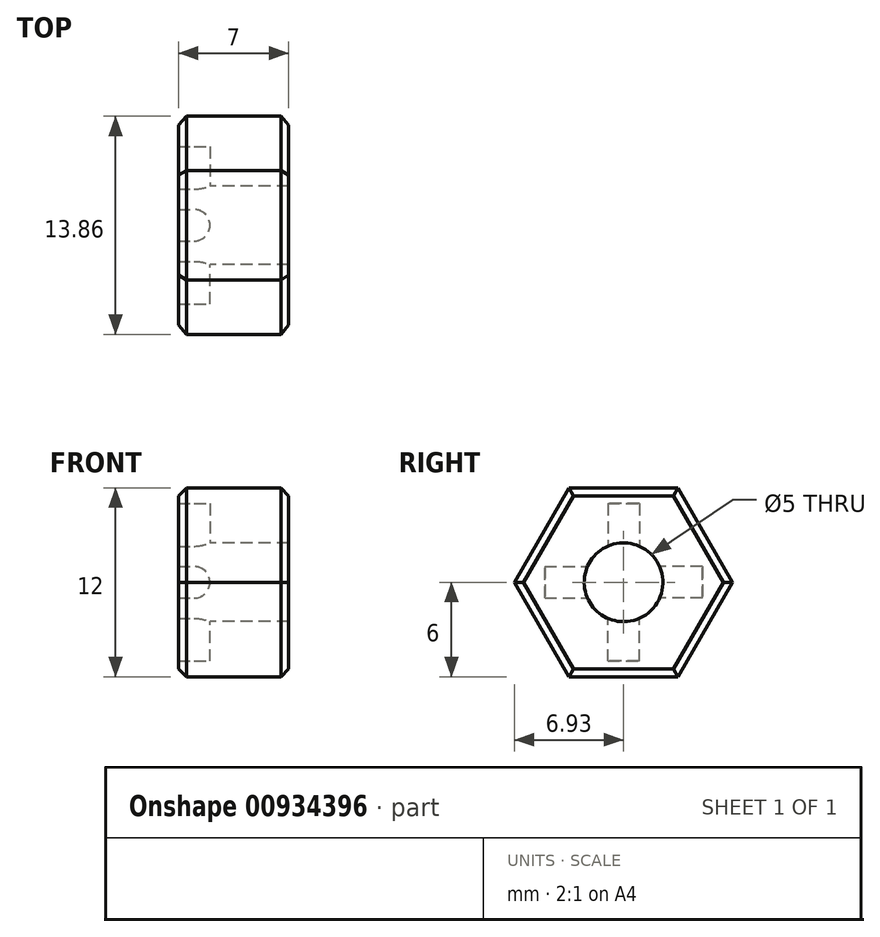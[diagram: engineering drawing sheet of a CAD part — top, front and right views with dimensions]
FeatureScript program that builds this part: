
annotation { "Feature Type Name" : "Feature", "Feature Type Description" : "" }
export const myFeature = defineFeature(function(context is Context, id is Id, definition is map)
    precondition{}
    {
        {
            var Q0;
            Q0=qCreatedBy(makeId("Right.planeOp"),FACE);
            var sketch = newSketch(context, id + "F0", { "sketchPlane" : qUnion([Q0])});
            skCircle(sketch, "E0.cCircle", {"center": v(0, 0) * mm, "radius": 6 * mm, "construction": true});
            skLineSegment(sketch, "E0.0", {"start": v(-3.46, 6) * mm, "end": v(3.46, 6) * mm});
            skLineSegment(sketch, "E0.1", {"start": v(3.46, 6) * mm, "end": v(6.93, 0) * mm});
            skLineSegment(sketch, "E0.2", {"start": v(6.93, 0) * mm, "end": v(3.46, -6) * mm});
            skLineSegment(sketch, "E0.3", {"start": v(3.46, -6) * mm, "end": v(-3.46, -6) * mm});
            skLineSegment(sketch, "E0.4", {"start": v(-3.46, -6) * mm, "end": v(-6.93, 0) * mm});
            skLineSegment(sketch, "E0.5", {"start": v(-6.93, 0) * mm, "end": v(-3.46, 6) * mm});
            skPoint(sketch, "E0.0.midPoint", {"position": v(0, 6) * mm});
            skCircle(sketch, "E1", {"center": v(0, 0) * mm, "radius": 2.5 * mm});
            skSolve(sketch);
        }
        {
            var Q0;
            Q0=qCreatedBy(makeId("Front.planeOp"),FACE);
            var sketch = newSketch(context, id + "F1", { "sketchPlane" : qUnion([Q0])});
            skCircle(sketch, "E2", {"center": v(0, 0) * mm, "radius": 1 * mm});
            skSolve(sketch);
        }
        {
            var Q0;
            Q0=qCreatedBy(makeId("Top.planeOp"),FACE);
            var sketch = newSketch(context, id + "F2", { "sketchPlane" : qUnion([Q0])});
            skCircle(sketch, "E3", {"center": v(0, 0) * mm, "radius": 1 * mm});
            skSolve(sketch);
        }
        {
            var Q0;
            Q0=makeQuery(id+"F0.imprint","IMPRINT",FACE,{"disambiguationData":[TD([[makeQuery(id+"F0.imprint","IMPRINT",EDGE,{"derivedFrom":sQuery(id+"F0.wireOp",EDGE,"E0.0")}),-1.0]])]});
            extrude(context, id + "F3", {"entities" : qUnion([Q0]), "depth" : 6 * mm, "offsetDistance" : 25 * mm});
        }
        {
            var Q0;
            Q0=makeQuery(id+"F1.imprint","IMPRINT",FACE,{"disambiguationData":[TD([[makeQuery(id+"F1.imprint","IMPRINT",EDGE,{"derivedFrom":sQuery(id+"F1.wireOp",EDGE,"E2")}),1.0]])]});
            extrude(context, id + "F4", {"entities" : qUnion([Q0]), "operationType" : NewBodyOperationType.REMOVE, "oppositeDirection" : true, "depth" : 5 * mm, "offsetDistance" : 25 * mm});
        }
        {
            var Q0;
            Q0=qSketchRegion(id+"F1",true);
            extrude(context, id + "F5", {"entities" : qUnion([Q0]), "operationType" : NewBodyOperationType.REMOVE, "depth" : 5 * mm, "offsetDistance" : 25 * mm});
        }
        {
            var Q0;
            Q0=qSketchRegion(id+"F2",true);
            extrude(context, id + "F6", {"entities" : qUnion([Q0]), "operationType" : NewBodyOperationType.REMOVE, "oppositeDirection" : true, "depth" : 5 * mm, "offsetDistance" : 25 * mm});
        }
        {
            var Q0;
            Q0=qSketchRegion(id+"F2",true);
            extrude(context, id + "F7", {"entities" : qUnion([Q0]), "operationType" : NewBodyOperationType.REMOVE, "depth" : 5 * mm, "offsetDistance" : 25 * mm});
        }
        {
            var Q0;
            Q0=makeQuery(id+"F3.opExtrude","CAP_EDGE",EDGE,{"disambiguationData":[OSD([sQuery(id+"F0.wireOp",EDGE,"E0.3")])],"isStart":false});
            var Q1;
            Q1=makeQuery(id+"F3.opExtrude","CAP_EDGE",EDGE,{"disambiguationData":[OSD([sQuery(id+"F0.wireOp",EDGE,"E0.2")])],"isStart":false});
            var Q2;
            Q2=makeQuery(id+"F3.opExtrude","CAP_EDGE",EDGE,{"disambiguationData":[OSD([sQuery(id+"F0.wireOp",EDGE,"E0.1")])],"isStart":false});
            var Q3;
            Q3=makeQuery(id+"F3.opExtrude","CAP_EDGE",EDGE,{"disambiguationData":[OSD([sQuery(id+"F0.wireOp",EDGE,"E0.0")])],"isStart":false});
            var Q4;
            Q4=makeQuery(id+"F3.opExtrude","CAP_EDGE",EDGE,{"disambiguationData":[OSD([sQuery(id+"F0.wireOp",EDGE,"E0.5")])],"isStart":false});
            var Q5;
            Q5=makeQuery(id+"F3.opExtrude","CAP_EDGE",EDGE,{"disambiguationData":[OSD([sQuery(id+"F0.wireOp",EDGE,"E0.4")])],"isStart":false});
            chamfer(context, id + "F8", {"entities" : qUnion([Q0, Q1, Q2, Q3, Q4, Q5]), "width" : 0.5 * mm, "tangentPropagation" : true});
        }
        {
            var Q0;
            Q0=makeQuery(id+"F3.opExtrude","CAP_FACE",FACE,{"disambiguationData":[OSD([sQuery(id+"F0.wireOp",EDGE,"E0.0"),sQuery(id+"F0.wireOp",EDGE,"E0.1"),sQuery(id+"F0.wireOp",EDGE,"E0.2"),sQuery(id+"F0.wireOp",EDGE,"E0.3"),sQuery(id+"F0.wireOp",EDGE,"E0.4"),sQuery(id+"F0.wireOp",EDGE,"E0.5"),sQuery(id+"F0.wireOp",EDGE,"E1")])],"isStart":true});
            extrude(context, id + "F9", {"entities" : qUnion([Q0]), "operationType" : NewBodyOperationType.ADD, "depth" : 1 * mm, "offsetDistance" : 25 * mm});
        }
        {
            var Q0;
            Q0=makeQuery(id+"F9.opExtrude","CAP_EDGE",EDGE,{"disambiguationData":[OSD([sQuery(id+"F0.wireOp",EDGE,"E0.4")])],"isStart":false});
            var Q1;
            Q1=makeQuery(id+"F9.opExtrude","CAP_EDGE",EDGE,{"disambiguationData":[OSD([sQuery(id+"F0.wireOp",EDGE,"E0.2")])],"isStart":false});
            var Q2;
            Q2=makeQuery(id+"F9.opExtrude","CAP_EDGE",EDGE,{"disambiguationData":[OSD([sQuery(id+"F0.wireOp",EDGE,"E0.3")])],"isStart":false});
            var Q3;
            Q3=makeQuery(id+"F9.opExtrude","CAP_EDGE",EDGE,{"disambiguationData":[OSD([sQuery(id+"F0.wireOp",EDGE,"E0.0")])],"isStart":false});
            var Q4;
            Q4=makeQuery(id+"F9.opExtrude","CAP_EDGE",EDGE,{"disambiguationData":[OSD([sQuery(id+"F0.wireOp",EDGE,"E0.1")])],"isStart":false});
            var Q5;
            Q5=makeQuery(id+"F9.opExtrude","CAP_EDGE",EDGE,{"disambiguationData":[OSD([sQuery(id+"F0.wireOp",EDGE,"E0.5")])],"isStart":false});
            chamfer(context, id + "F10", {"entities" : qUnion([Q0, Q1, Q2, Q3, Q4, Q5]), "width" : 0.5 * mm, "tangentPropagation" : true});
        }
    });
